# Revit family: Shower-Shower_Column_Kit-KOHLER-Urbanity-K-23751T_1
name_source: partatom
category: Plumbing Fixtures
units: mm (PartAtom-declared; Revit-internal decimal feet)

## family parameters
Cut with Voids When Loaded = No
Host = Face
OmniClass Number = 23.31.17.00
OmniClass Title = Showers
Part Type = Normal
Room Calculation Point = No
Round Connector Dimension = Use Diameter
Shared = No

## types (5) — shared parameters
ADA Compliant = No
Assembly Code = D2010700
CW Connection = Yes
Cold Water Inlet = Cold Water Inlet
Date Modified = 04/14/2023
Default Elevation = 42"
Description = Abbe Thermostat Double Rain Shower Column – multi-functional overhead shower
Drain Included = No
Flow Rate = 0 GPM
HW Connection = Yes
Height = 47 5/8"
Hot Water Inlet = Hot Water Inlet
Length = 21 15/16"
Manufacturer = Kohler Co.
Master Format 2014 = 22 42 23
Master Format 2014 Name = Residential Showers
Material = Premium Metal Construction
Panel Thickness = 0"
Pressure = 0.00 psi
Product Documentation Link = https://files.kohler.com.cn
Product Name = Urbanity
URL = http://www.kohler.com.cn
Vent Connection = No
Waste Connection = No
Waste Water Outlet = Waste Water Outlet
WaterSense Certified = No
Width = 13 3/16"

## per-type parameters (varying)
| type | Finish | Model | Nozzle Finish | Product Page URL | Secondary Finish | Type |
| 2MB-Vibrant Brushed Moderne Brass | Kohler-Metal-2MB-Vibrant_Brushed_Moderne_Brass | K-23751T-9-2MB | Kohler-Plastic-BL-Matte_Black | https://www.kohler.com.cn | Kohler-Plastic-BL-Matte_Black | 1 |
| BL-Matte Black | Kohler-Metal-BL-Matte_Black | K-23751T-9-BL | Kohler-Plastic-BL-Matte_Black | https://www.kohler.com.cn | Kohler-Plastic-BL-Matte_Black | 2 |
| CP-Polished Chrome | Kohler-Metal-CP-Polished_Chrome | K-23751T-9-CP | Kohler-Plastic-0-White | https://www.kohler.com.cn | Kohler-Plastic-0-White | 3 |
| CY-Cloud Gray | Kohler-Metal-CY-Cloud_Gray | K-23751T-9-CY | Kohler-Plastic-BL-Matte_Black | https://www.kohler.com.cn | Kohler-Plastic-BL-Matte_Black | 4 |
| RGD-Polished Rose Gold | Kohler-Metal-RGD-Polished_Rose_Gold | K-23751T-9-RGD | Kohler-Plastic-0-White |  | Kohler-Plastic-0-White | 5 |

## geometry (parser evidence)
native form markers: Sweep x5
no freeform markers — native parametric forms only
